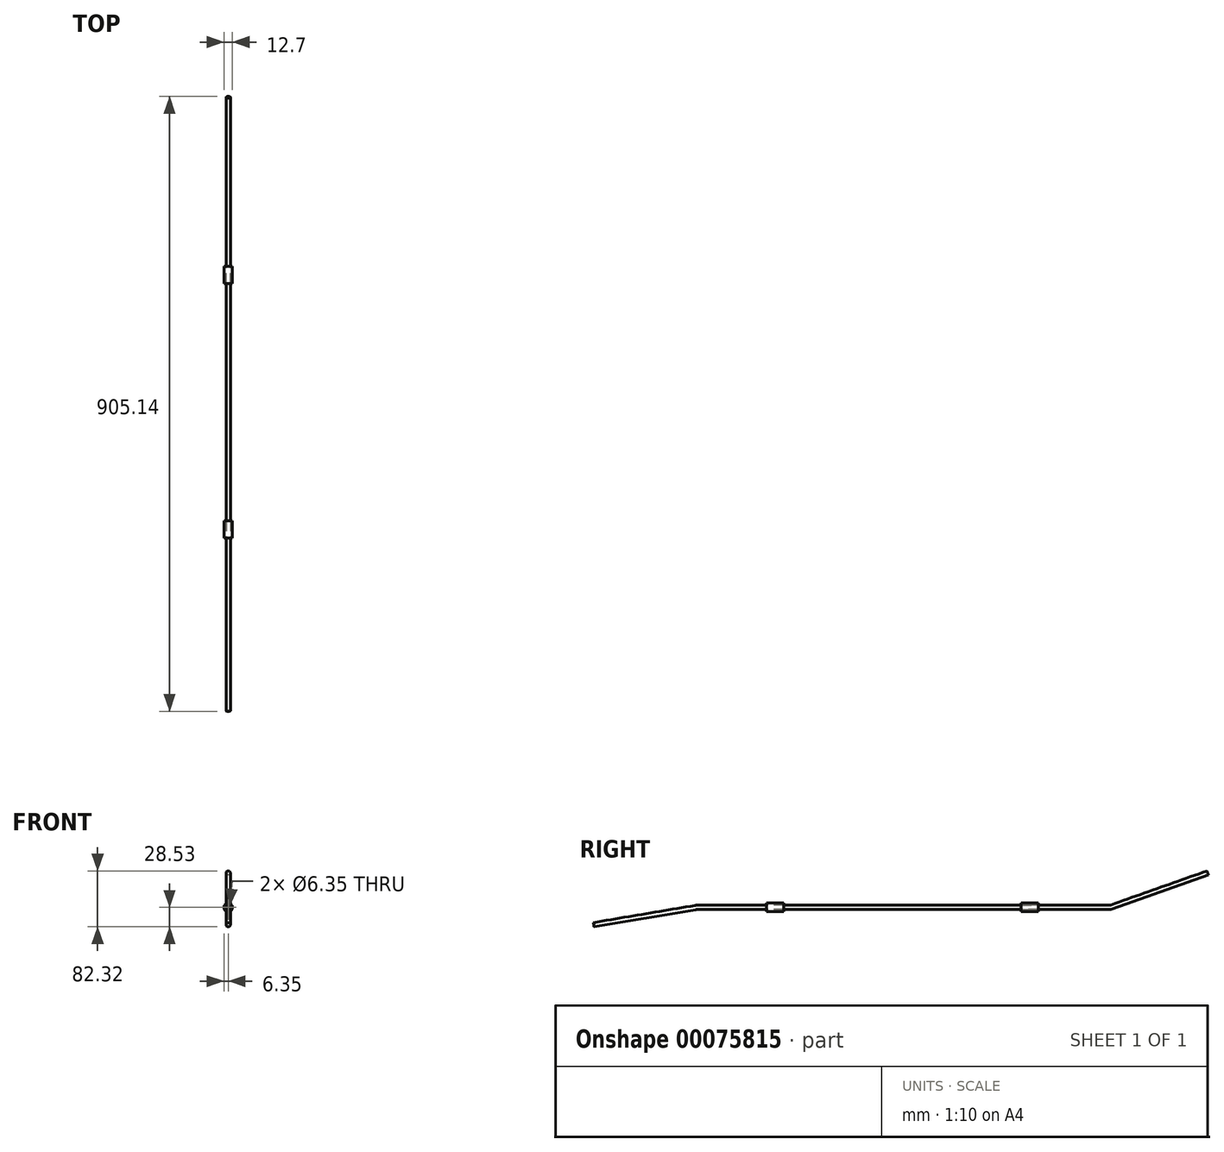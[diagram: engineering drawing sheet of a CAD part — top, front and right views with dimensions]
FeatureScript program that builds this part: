
annotation { "Feature Type Name" : "Feature", "Feature Type Description" : "" }
export const myFeature = defineFeature(function(context is Context, id is Id, definition is map)
    precondition{}
    {
        {
            var Q0;
            Q0=qCreatedBy(makeId("Right.planeOp"),FACE);
            var sketch = newSketch(context, id + "F0", { "sketchPlane" : qUnion([Q0])});
            skLineSegment(sketch, "E0", {"start": v(-303.18, 0) * mm, "end": v(303.18, 0) * mm});
            skLineSegment(sketch, "E1", {"start": v(307.41, 0.73) * mm, "end": v(449.04, 50.8) * mm});
            skLineSegment(sketch, "E2", {"start": v(-305.3, -0.18) * mm, "end": v(-454.51, -25.4) * mm});
            skPoint(sketch, "E3.visualSharp", {"position": v(305.36, 0) * mm});
            skArc(sketch, "E3.filletArc", {"start": v(303.18, 0) * mm, "mid": v(305.33, 0.18) * mm, "end": v(307.41, 0.73) * mm});
            skPoint(sketch, "E4.visualSharp", {"position": v(-304.24, 0) * mm});
            skArc(sketch, "E4.filletArc", {"start": v(-303.18, 0) * mm, "mid": v(-304.24, -0.04) * mm, "end": v(-305.3, -0.18) * mm});
            skSolve(sketch);
        }
        {
            var Q0;
            Q0=sQuery(id+"F0.wireOp",VERTEX,"E1.end");
            var Q1;
            Q1=sQuery(id+"F0.wireOp",EDGE,"E1");
            cPlane(context, id + "F1", {"entities" : qUnion([Q0, Q1]), "cplaneType" : CPlaneType.LINE_POINT, "offset" : 150 * mm, "width" : 150 * mm, "height" : 150 * mm});
        }
        {
            var Q0;
            Q0=qCreatedBy(id+"F1.planeOp",FACE);
            var sketch = newSketch(context, id + "F2", { "sketchPlane" : qUnion([Q0])});
            skPoint(sketch, "E5.0", {"position": v(0, -101.79) * mm});
            skCircle(sketch, "E6", {"center": v(0, -101.79) * mm, "radius": 3.18 * mm});
            skSolve(sketch);
        }
        {
            var Q0;
            Q0=makeQuery(id+"F2.imprint","IMPRINT",FACE,{"disambiguationData":[TD([[makeQuery(id+"F2.imprint","IMPRINT",EDGE,{"derivedFrom":sQuery(id+"F2.wireOp",EDGE,"E6")}),1.0]])]});
            var Q1;
            Q1=sQuery(id+"F0.wireOp",EDGE,"E1");
            var Q2;
            Q2=sQuery(id+"F0.wireOp",EDGE,"E3.filletArc");
            var Q3;
            Q3=sQuery(id+"F0.wireOp",EDGE,"E0");
            var Q4;
            Q4=sQuery(id+"F0.wireOp",EDGE,"E4.filletArc");
            var Q5;
            Q5=sQuery(id+"F0.wireOp",EDGE,"E2");
            sweep(context, id + "F3", {"profiles" : qUnion([Q0]), "path" : qUnion([Q1, Q2, Q3, Q4, Q5])});
        }
        {
            var Q0;
            Q0=qCreatedBy(makeId("Front.planeOp"),FACE);
            var sketch = newSketch(context, id + "F4", { "sketchPlane" : qUnion([Q0])});
            skCircle(sketch, "E7", {"center": v(0, 0) * mm, "radius": 3.18 * mm});
            skCircle(sketch, "E8", {"center": v(0, 0) * mm, "radius": 6.35 * mm});
            skSolve(sketch);
        }
        {
            var Q0;
            Q0 = qSketchRegion(id + "F4", true);
            extrude(context, id + "F5", {"entities" : qUnion([Q0]), "depth" : 25.4 * mm});
        }
        {
            var Q0;
            Q0=makeQuery(id+"F5.opExtrude","SWEPT_BODY",BODY,{"disambiguationData":[OSD([sQuery(id+"F4.wireOp",EDGE,"E7"),sQuery(id+"F4.wireOp",EDGE,"E8")])]});
            transform(context, id + "F6", {"entities" : qUnion([Q0]), "transformType" : TransformType.TRANSLATION_3D, "dx" : 0 * mm, "dy" : 200 * mm, "dz" : 0 * mm, "makeCopy" : false});
        }
        {
            var Q0;
            Q0=makeQuery(id+"F5.opExtrude","SWEPT_BODY",BODY,{"disambiguationData":[OSD([sQuery(id+"F4.wireOp",EDGE,"E7"),sQuery(id+"F4.wireOp",EDGE,"E8")])]});
            var Q1;
            Q1=qCreatedBy(makeId("Front.planeOp"),FACE);
            mirror(context, id + "F7", {"entities" : qUnion([Q0]), "mirrorPlane" : qUnion([Q1])});
        }
        {
            var Q0;
            Q0=qCreatedBy(makeId("Front.planeOp"),FACE);
            var sketch = newSketch(context, id + "F8", { "sketchPlane" : qUnion([Q0])});
            skLineSegment(sketch, "E9", {"start": v(0, 0) * mm, "end": v(-6.35, 0) * mm});
            skSolve(sketch);
        }
    });
